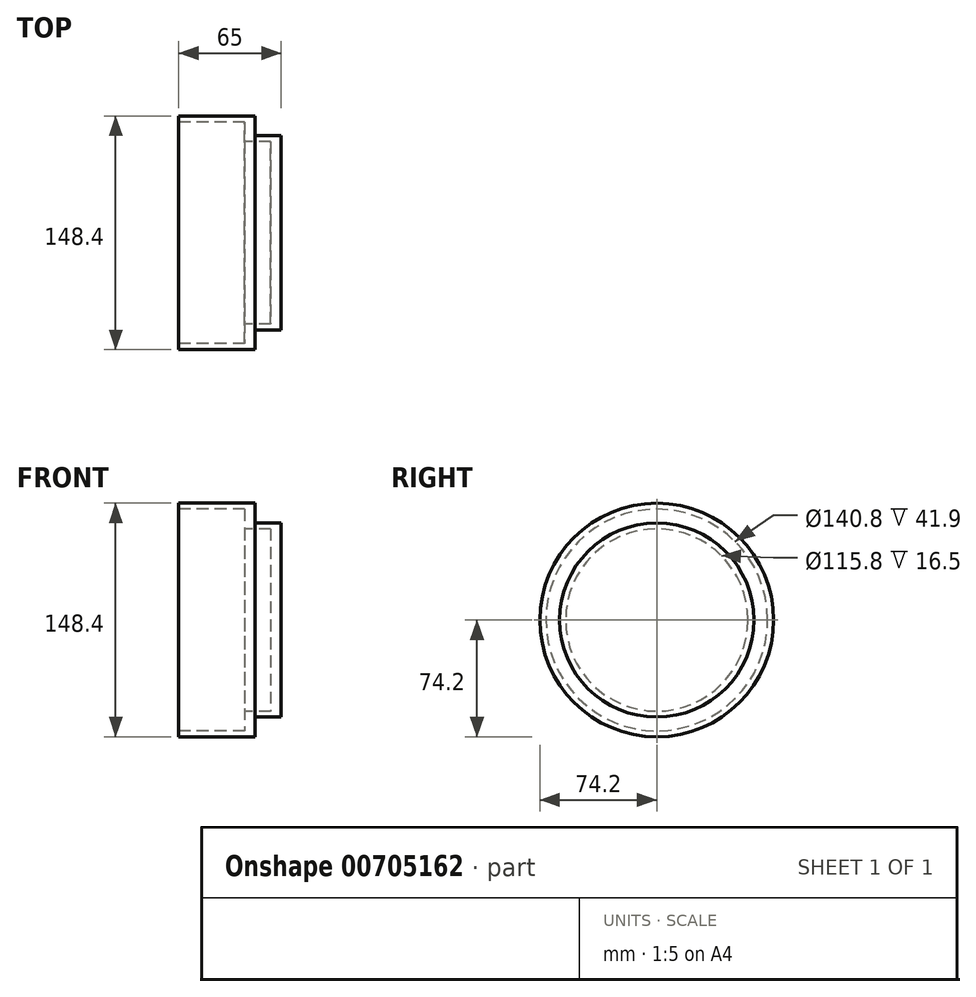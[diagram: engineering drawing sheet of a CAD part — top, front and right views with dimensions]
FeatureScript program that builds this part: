
annotation { "Feature Type Name" : "Feature", "Feature Type Description" : "" }
export const myFeature = defineFeature(function(context is Context, id is Id, definition is map)
    precondition{}
    {
        {
            var Q0;
            Q0=qCreatedBy(makeId("Front.planeOp"),FACE);
            var sketch = newSketch(context, id + "F0", { "sketchPlane" : qUnion([Q0])});
            skLineSegment(sketch, "E0", {"start": v(0, 0) * mm, "end": v(0, 61.7) * mm});
            skLineSegment(sketch, "E1", {"start": v(0, 61.7) * mm, "end": v(-16.5, 61.7) * mm});
            skLineSegment(sketch, "E2", {"start": v(-16.5, 74.2) * mm, "end": v(-16.5, 61.7) * mm});
            skLineSegment(sketch, "E3", {"start": v(-16.5, 74.2) * mm, "end": v(-65, 74.2) * mm});
            skLineSegment(sketch, "E4", {"start": v(-65, 74.2) * mm, "end": v(-65, 70.4) * mm});
            skLineSegment(sketch, "E5", {"start": v(-65, 70.4) * mm, "end": v(-23.1, 70.4) * mm});
            skLineSegment(sketch, "E6", {"start": v(-23.1, 57.9) * mm, "end": v(-23.1, 70.4) * mm});
            skLineSegment(sketch, "E7", {"start": v(-23.1, 57.9) * mm, "end": v(-6.6, 57.9) * mm});
            skLineSegment(sketch, "E8", {"start": v(-6.6, 57.9) * mm, "end": v(-6.6, 0) * mm});
            skLineSegment(sketch, "E9", {"start": v(-6.6, 0) * mm, "end": v(0, 0) * mm});
            skSolve(sketch);
        }
        {
            var Q0;
            Q0=makeQuery(id+"F0.imprint","IMPRINT",FACE,{"disambiguationData":[TD([[makeQuery(id+"F0.imprint","IMPRINT",EDGE,{"derivedFrom":sQuery(id+"F0.wireOp",EDGE,"E0")}),1.0]])]});
            var Q1;
            Q1=sQuery(id+"F0.wireOp",EDGE,"E9");
            revolve(context, id + "F1", {"surfaceOperationType" : NewSurfaceOperationType.NEW, "entities" : qUnion([Q0]), "axis" : qUnion([Q1]), "revolveType" : RevolveType.FULL});
        }
    });
